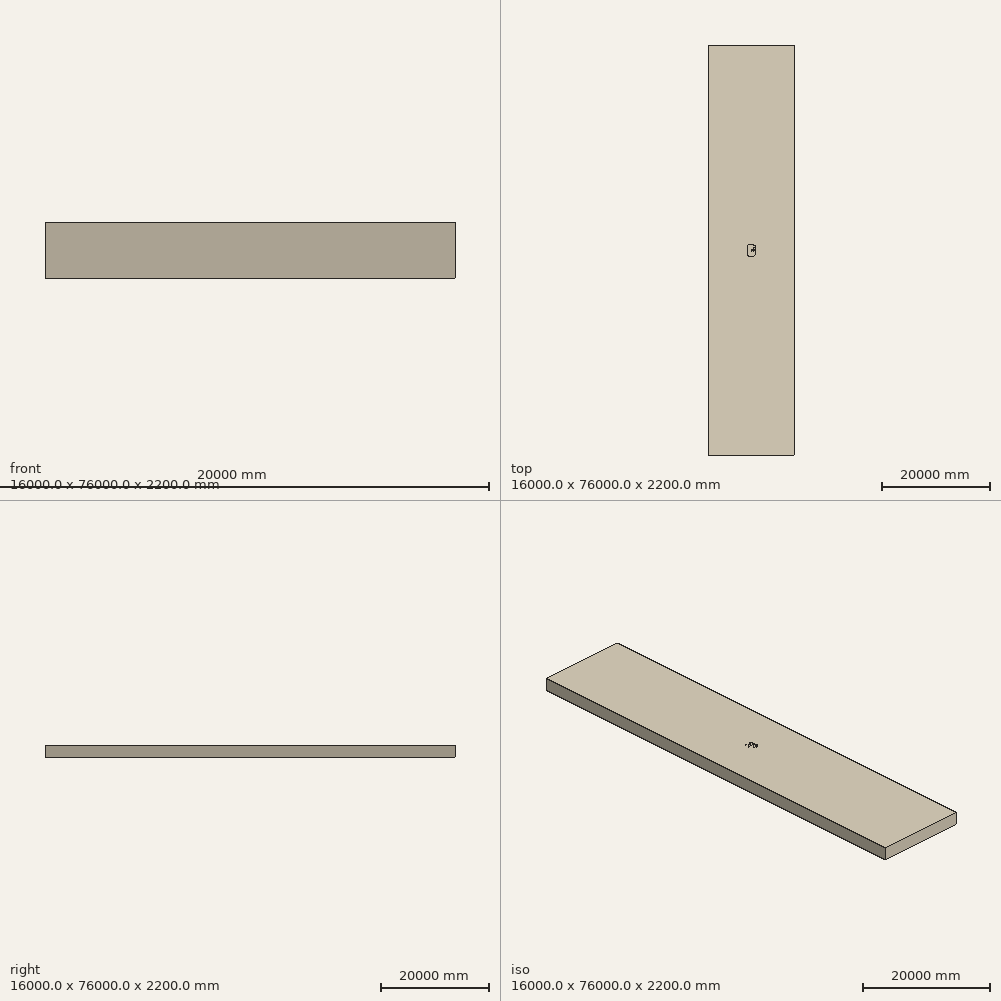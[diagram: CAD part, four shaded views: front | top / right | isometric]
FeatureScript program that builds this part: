
annotation { "Feature Type Name" : "Feature", "Feature Type Description" : "" }
export const myFeature = defineFeature(function(context is Context, id is Id, definition is map)
    precondition{}
    {
        {
            var Q0;
            Q0=qCreatedBy(makeId("Top.planeOp"),FACE);
            var sketch = newSketch(context, id + "F0", { "sketchPlane" : qUnion([Q0])});
            skLineSegment(sketch, "E0.bottom", {"start": v(-800, 1050) * mm, "end": v(800, 1050) * mm});
            skLineSegment(sketch, "E0.top", {"start": v(-800, -1050) * mm, "end": v(800, -1050) * mm});
            skLineSegment(sketch, "E0.left", {"start": v(-800, 1050) * mm, "end": v(-800, -1050) * mm});
            skLineSegment(sketch, "E0.right", {"start": v(800, 1050) * mm, "end": v(800, -1050) * mm});
            skPoint(sketch, "E0.middle", {"position": v(0, 0) * mm});
            skSolve(sketch);
        }
        {
            var Q0;
            Q0=makeQuery(id+"F0.imprint","IMPRINT",FACE,{"disambiguationData":[TD([[makeQuery(id+"F0.imprint","IMPRINT",EDGE,{"derivedFrom":sQuery(id+"F0.wireOp",EDGE,"E0.bottom")}),-1.0]])]});
            extrude(context, id + "F1", {"entities" : qUnion([Q0]), "depth" : 2200 * mm});
        }
        {
            var Q0;
            Q0=makeQuery(id+"F1.opExtrude","SWEPT_EDGE",EDGE,{"disambiguationData":[OSD([sQuery(id+"F0.wireOp",EDGE,"E0.top"),sQuery(id+"F0.wireOp",EDGE,"E0.right")])]});
            var Q1;
            Q1=makeQuery(id+"F1.opExtrude","SWEPT_EDGE",EDGE,{"disambiguationData":[OSD([sQuery(id+"F0.wireOp",EDGE,"E0.bottom"),sQuery(id+"F0.wireOp",EDGE,"E0.right")])]});
            var Q2;
            Q2=makeQuery(id+"F1.opExtrude","SWEPT_EDGE",EDGE,{"disambiguationData":[OSD([sQuery(id+"F0.wireOp",EDGE,"E0.top"),sQuery(id+"F0.wireOp",EDGE,"E0.left")])]});
            var Q3;
            Q3=makeQuery(id+"F1.opExtrude","SWEPT_EDGE",EDGE,{"disambiguationData":[OSD([sQuery(id+"F0.wireOp",EDGE,"E0.bottom"),sQuery(id+"F0.wireOp",EDGE,"E0.left")])]});
            fillet(context, id + "F2", {"entities" : qUnion([Q0, Q1, Q2, Q3]), "radius" : 500 * mm, "tangentPropagation" : true, "allowEdgeOverflow" : false});
        }
        {
            var Q0;
            Q0=makeQuery(id+"F1.opExtrude","CAP_FACE",FACE,{"disambiguationData":[OSD([sQuery(id+"F0.wireOp",EDGE,"E0.bottom"),sQuery(id+"F0.wireOp",EDGE,"E0.top"),sQuery(id+"F0.wireOp",EDGE,"E0.left"),sQuery(id+"F0.wireOp",EDGE,"E0.right")])],"isStart":false});
            var sketch = newSketch(context, id + "F3", { "sketchPlane" : qUnion([Q0])});
            skLineSegment(sketch, "E1.bottom", {"start": v(8000, -38000) * mm, "end": v(-8000, -38000) * mm});
            skLineSegment(sketch, "E1.top", {"start": v(8000, 38000) * mm, "end": v(-8000, 38000) * mm});
            skLineSegment(sketch, "E1.left", {"start": v(8000, -38000) * mm, "end": v(8000, 38000) * mm});
            skLineSegment(sketch, "E1.right", {"start": v(-8000, -38000) * mm, "end": v(-8000, 38000) * mm});
            skPoint(sketch, "E1.middle", {"position": v(0, 0) * mm});
            skSolve(sketch);
        }
        {
            var Q0;
            Q0 = qSketchRegion(id + "F3", true);
            extrude(context, id + "F4", {"entities" : qUnion([Q0]), "operationType" : NewBodyOperationType.ADD, "oppositeDirection" : true, "depth" : 2200 * mm});
        }
        {
            var Q0;
            Q0=makeQuery(id+"F4.boolean.opBoolean","MERGE",FACE,{"derivedFrom":[makeQuery(id+"F1.opExtrude","CAP_FACE",FACE,{"disambiguationData":[OSD([sQuery(id+"F0.wireOp",EDGE,"E0.bottom"),sQuery(id+"F0.wireOp",EDGE,"E0.top"),sQuery(id+"F0.wireOp",EDGE,"E0.left"),sQuery(id+"F0.wireOp",EDGE,"E0.right")])],"isStart":true}),makeQuery(id+"F4.opExtrude","CAP_FACE",FACE,{"disambiguationData":[OSD([sQuery(id+"F3.wireOp",EDGE,"E1.bottom"),sQuery(id+"F3.wireOp",EDGE,"E1.top"),sQuery(id+"F3.wireOp",EDGE,"E1.left"),sQuery(id+"F3.wireOp",EDGE,"E1.right")])],"isStart":false})]});
            var Q1;
            Q1=makeQuery(id+"F1.opExtrude","SWEPT_BODY",BODY,{"disambiguationData":[OSD([sQuery(id+"F0.wireOp",EDGE,"E0.bottom"),sQuery(id+"F0.wireOp",EDGE,"E0.top"),sQuery(id+"F0.wireOp",EDGE,"E0.left"),sQuery(id+"F0.wireOp",EDGE,"E0.right")])]});
            shell(context, id + "F5", {"isHollow" : true, "entities" : qUnion([Q0]), "parts" : qUnion([Q1]), "thickness" : 2.5 * mm});
        }
        {
            var Q0;
            Q0=makeQuery(id+"F4.boolean.opBoolean","MERGE",FACE,{"derivedFrom":[makeQuery(id+"F1.opExtrude","CAP_FACE",FACE,{"disambiguationData":[OSD([sQuery(id+"F0.wireOp",EDGE,"E0.bottom"),sQuery(id+"F0.wireOp",EDGE,"E0.top"),sQuery(id+"F0.wireOp",EDGE,"E0.left"),sQuery(id+"F0.wireOp",EDGE,"E0.right")])],"isStart":true}),makeQuery(id+"F4.opExtrude","CAP_FACE",FACE,{"disambiguationData":[OSD([sQuery(id+"F3.wireOp",EDGE,"E1.bottom"),sQuery(id+"F3.wireOp",EDGE,"E1.top"),sQuery(id+"F3.wireOp",EDGE,"E1.left"),sQuery(id+"F3.wireOp",EDGE,"E1.right")])],"isStart":false})]});
            var sketch = newSketch(context, id + "F6", { "sketchPlane" : qUnion([Q0])});
            skLineSegment(sketch, "E2.bottom", {"start": v(-800, 1050) * mm, "end": v(800, 1050) * mm});
            skLineSegment(sketch, "E2.top", {"start": v(-800, -1050) * mm, "end": v(800, -1050) * mm});
            skLineSegment(sketch, "E2.left", {"start": v(-800, 1050) * mm, "end": v(-800, -1050) * mm});
            skLineSegment(sketch, "E2.right", {"start": v(800, 1050) * mm, "end": v(800, -1050) * mm});
            skPoint(sketch, "E2.middle", {"position": v(0, 0) * mm});
            skSolve(sketch);
        }
        {
            var Q0;
            Q0 = qSketchRegion(id + "F6", true);
            extrude(context, id + "F7", {"entities" : qUnion([Q0]), "oppositeDirection" : true, "depth" : 2200 * mm});
        }
        {
            var Q0;
            Q0=makeQuery(id+"F7.opExtrude","SWEPT_EDGE",EDGE,{"disambiguationData":[OSD([sQuery(id+"F6.wireOp",EDGE,"E2.bottom"),sQuery(id+"F6.wireOp",EDGE,"E2.left")])]});
            var Q1;
            Q1=makeQuery(id+"F7.opExtrude","SWEPT_EDGE",EDGE,{"disambiguationData":[OSD([sQuery(id+"F6.wireOp",EDGE,"E2.top"),sQuery(id+"F6.wireOp",EDGE,"E2.left")])]});
            var Q2;
            Q2=makeQuery(id+"F7.opExtrude","SWEPT_EDGE",EDGE,{"disambiguationData":[OSD([sQuery(id+"F6.wireOp",EDGE,"E2.bottom"),sQuery(id+"F6.wireOp",EDGE,"E2.right")])]});
            var Q3;
            Q3=makeQuery(id+"F7.opExtrude","SWEPT_EDGE",EDGE,{"disambiguationData":[OSD([sQuery(id+"F6.wireOp",EDGE,"E2.top"),sQuery(id+"F6.wireOp",EDGE,"E2.right")])]});
            fillet(context, id + "F8", {"entities" : qUnion([Q0, Q1, Q2, Q3]), "radius" : 500 * mm, "tangentPropagation" : true, "allowEdgeOverflow" : false});
        }
    });
